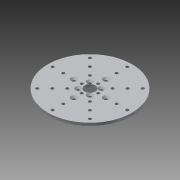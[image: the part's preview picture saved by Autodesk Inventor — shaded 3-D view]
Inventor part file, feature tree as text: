
AUTODESK INVENTOR PART (.ipt)
format: ipt  version: 2015 (Build 190159000, 159)  size: 285,184 bytes
history: native  units: in
note: dims shown in document units (in); Inventor stores cm internally (conversion verified against a paired STEP export)
features: hole x2, sketch x2, other x1, imported_body x1
ambient origin geometry x8: Origin, YZ Plane, XZ Plane, XY Plane, X Axis, Y Axis, Z Axis, Center Point
bodies: Solid1 (feature_tree)
feature tree (6):
  other  "User Library-585438.sat1"
  hole  "Hole1"  [1 undecoded]
  hole  "Hole2"  [1 undecoded]
  imported_body  "Base1"
  sketch  "Sketch2"  dims[d4=0.1406in d5=0.144in]
  sketch  "Sketch3"  dims[d6=0.1406in d7=0.1406in d8=0.144in d9=0.1406in d10=0.1406in d11=0.1406in d12=0.1406in d13=0.141in d14=0.75in d15=0.375in d16=0.25in d17=0.5635in d18=1.0in d19=0.8108in d20=0.144in d21=0.144in d22=0.144in d23=0.144in d24=0.144in d25=0.144in d27=0.144in d28=0.144in d29=0.145in d30=0.75in d31=0.375in d32=0.25in d33=0.5635in d34=1.0in d35=0.8108in]
note: 2 required parameter values undecoded (feature->parameter linkage not recoverable at this tier; creation-order binding heuristic only, values carry confidence <= 0.55)
